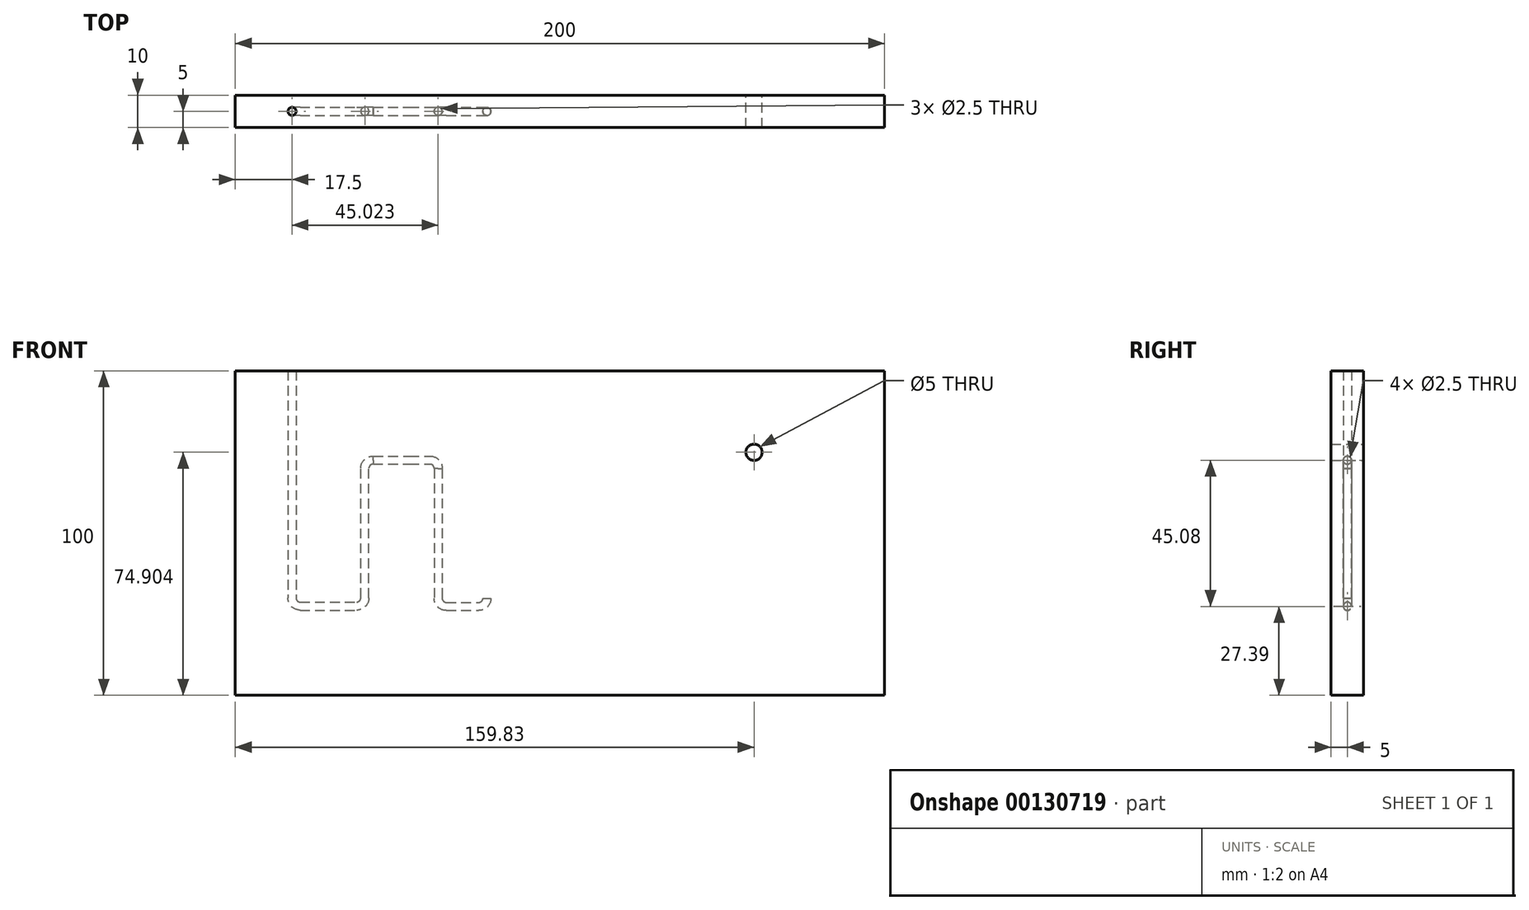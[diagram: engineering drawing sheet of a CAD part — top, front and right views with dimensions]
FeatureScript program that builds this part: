
annotation { "Feature Type Name" : "Feature", "Feature Type Description" : "" }
export const myFeature = defineFeature(function(context is Context, id is Id, definition is map)
    precondition{}
    {
        {
            var Q0;
            Q0=qCreatedBy(makeId("Front.planeOp"),FACE);
            var sketch = newSketch(context, id + "F0", { "sketchPlane" : qUnion([Q0])});
            skLineSegment(sketch, "E0.bottom", {"start": v(100, 50) * mm, "end": v(-100, 50) * mm});
            skLineSegment(sketch, "E0.top", {"start": v(100, -50) * mm, "end": v(-100, -50) * mm});
            skLineSegment(sketch, "E0.left", {"start": v(100, 50) * mm, "end": v(100, -50) * mm});
            skLineSegment(sketch, "E0.right", {"start": v(-100, 50) * mm, "end": v(-100, -50) * mm});
            skPoint(sketch, "E0.middle", {"position": v(0, 0) * mm});
            skLineSegment(sketch, "E1.bottom", {"start": v(95, 45) * mm, "end": v(-95, 45) * mm});
            skLineSegment(sketch, "E1.top", {"start": v(95, -45) * mm, "end": v(-95, -45) * mm});
            skLineSegment(sketch, "E1.left", {"start": v(95, 45) * mm, "end": v(95, -45) * mm});
            skLineSegment(sketch, "E1.right", {"start": v(-95, 45) * mm, "end": v(-95, -45) * mm});
            skLineSegment(sketch, "E2.bottom", {"start": v(40, 22.5) * mm, "end": v(85, 22.5) * mm});
            skLineSegment(sketch, "E2.top", {"start": v(40, -22.5) * mm, "end": v(85, -22.5) * mm});
            skLineSegment(sketch, "E2.left", {"start": v(40, 22.5) * mm, "end": v(40, -22.5) * mm});
            skLineSegment(sketch, "E2.right", {"start": v(85, 22.5) * mm, "end": v(85, -22.5) * mm});
            skLineSegment(sketch, "E3", {"start": v(-82.5, 63.41) * mm, "end": v(-82.5, -18.85) * mm});
            skLineSegment(sketch, "E4", {"start": v(-75.95, -22.5) * mm, "end": v(-62.58, -22.5) * mm});
            skLineSegment(sketch, "E5", {"start": v(-82.5, -18.85) * mm, "end": v(-82.5, -20) * mm});
            skArc(sketch, "E6", {"start": v(-82.5, -20) * mm, "mid": v(-81.77, -21.77) * mm, "end": v(-80, -22.5) * mm});
            skPoint(sketch, "E7.orphan", {"position": v(-82.5, -22.5) * mm});
            skLineSegment(sketch, "E8", {"start": v(-75.95, -22.5) * mm, "end": v(-80, -22.5) * mm});
            skLineSegment(sketch, "E9", {"start": v(-37.48, 9) * mm, "end": v(-37.48, -20.11) * mm});
            skLineSegment(sketch, "E10", {"start": v(-34.98, -22.61) * mm, "end": v(-24.98, -22.61) * mm});
            skArc(sketch, "E11", {"start": v(-37.48, -20.11) * mm, "mid": v(-36.74, -21.88) * mm, "end": v(-34.98, -22.61) * mm});
            skLineSegment(sketch, "E12", {"start": v(-24.98, -22.61) * mm, "end": v(-24.98, -22.61) * mm});
            skLineSegment(sketch, "E13", {"start": v(-22.48, -7.76) * mm, "end": v(-22.48, 19.9) * mm});
            skArc(sketch, "E14", {"start": v(-19.98, 22.4) * mm, "mid": v(-21.74, 21.67) * mm, "end": v(-22.48, 19.9) * mm});
            skPoint(sketch, "E15.orphan", {"position": v(-22.49, 22.48) * mm});
            skPoint(sketch, "E16.endSnap0", {"position": v(-4.99, 24.98) * mm});
            skLineSegment(sketch, "E17", {"start": v(-19.98, 22.4) * mm, "end": v(-7.48, 22.4) * mm});
            skLineSegment(sketch, "E18", {"start": v(-4.98, 19.9) * mm, "end": v(-4.98, -20.1) * mm});
            skArc(sketch, "E19", {"start": v(-4.98, 19.9) * mm, "mid": v(-5.7, 21.67) * mm, "end": v(-7.48, 22.4) * mm});
            skPoint(sketch, "E20.orphan", {"position": v(-4.98, 22.4) * mm});
            skLineSegment(sketch, "E21", {"start": v(-2.48, -22.6) * mm, "end": v(10.02, -22.6) * mm});
            skArc(sketch, "E22", {"start": v(-4.98, -20.1) * mm, "mid": v(-4.24, -21.86) * mm, "end": v(-2.48, -22.6) * mm});
            skPoint(sketch, "E23.orphan", {"position": v(-4.98, -22.6) * mm});
            skArc(sketch, "E24", {"start": v(10.02, -22.6) * mm, "mid": v(11.8, -21.86) * mm, "end": v(12.52, -20.1) * mm});
            skPoint(sketch, "E25.orphan", {"position": v(12.52, -22.6) * mm});
            skArc(sketch, "E26", {"start": v(15.01, 27.39) * mm, "mid": v(13.26, 26.66) * mm, "end": v(12.53, 24.9) * mm});
            skLineSegment(sketch, "E27", {"start": v(15.01, 27.39) * mm, "end": v(59.83, 27.4) * mm});
            skLineSegment(sketch, "E28", {"start": v(12.53, 24.9) * mm, "end": v(12.52, -20.1) * mm});
            skLineSegment(sketch, "E29", {"start": v(62.5, 22.5) * mm, "end": v(62.5, -58.86) * mm});
            skLineSegment(sketch, "E30", {"start": v(-80, -20) * mm, "end": v(-62.5, -20) * mm});
            skLineSegment(sketch, "E31", {"start": v(15.01, 24.9) * mm, "end": v(59.83, 24.9) * mm});
            skCircle(sketch, "E32", {"center": v(59.83, 24.9) * mm, "radius": 2.5 * mm});
            skPoint(sketch, "E33.orphan", {"position": v(62.5, 27.4) * mm});
            skLineSegment(sketch, "E34", {"start": v(-60.08, -20) * mm, "end": v(-60.08, 19.97) * mm});
            skArc(sketch, "E35", {"start": v(-62.58, -22.5) * mm, "mid": v(-60.81, -21.77) * mm, "end": v(-60.08, -20) * mm});
            skArc(sketch, "E36", {"start": v(-60.08, 19.97) * mm, "mid": v(-59.31, 21.78) * mm, "end": v(-57.47, 22.47) * mm});
            skLineSegment(sketch, "E37", {"start": v(-37.48, 9) * mm, "end": v(-37.48, 19.86) * mm});
            skArc(sketch, "E38", {"start": v(-39.97, 22.47) * mm, "mid": v(-38.17, 21.7) * mm, "end": v(-37.48, 19.86) * mm});
            skLineSegment(sketch, "E39", {"start": v(-57.47, 22.47) * mm, "end": v(-52.28, 22.47) * mm});
            skLineSegment(sketch, "E40", {"start": v(-52.28, 22.47) * mm, "end": v(-46.34, 22.47) * mm});
            skLineSegment(sketch, "E41", {"start": v(-46.34, 22.47) * mm, "end": v(-39.97, 22.47) * mm});
            skArc(sketch, "E42", {"start": v(-24.98, -22.61) * mm, "mid": v(-23.2, -21.87) * mm, "end": v(-22.48, -20.1) * mm});
            skLineSegment(sketch, "E43", {"start": v(-22.48, -20.1) * mm, "end": v(-22.48, -7.76) * mm});
            skSolve(sketch);
        }
        {
            var Q0;
            Q0=qCreatedBy(makeId("Top.planeOp"),FACE);
            var Q1;
            Q1=sQuery(id+"F0.wireOp",VERTEX,"E3.start");
            cPlane(context, id + "F1", {"entities" : qUnion([Q0, Q1]), "cplaneType" : CPlaneType.PLANE_POINT, "offset" : 25 * mm, "width" : 150 * mm, "height" : 150 * mm});
        }
        {
            var Q0;
            Q0=qCreatedBy(id+"F1.planeOp",FACE);
            var sketch = newSketch(context, id + "F2", { "sketchPlane" : qUnion([Q0])});
            skCircle(sketch, "E44", {"center": v(-82.5, 0) * mm, "radius": 1.25 * mm});
            skSolve(sketch);
        }
        {
            var Q0;
            {var subQ6=sQuery(id+"F0.wireOp",EDGE,"E0.right");Q0=makeQuery(id+"F0.imprint","IMPRINT",FACE,{"disambiguationData":[TD([[makeQuery(id+"F0.imprint","IMPRINT",EDGE,{"derivedFrom":subQ6}),1.0]])]});}
            var Q1;
            {var subQ4=sQuery(id+"F0.wireOp",EDGE,"E1.right");Q1=makeQuery(id+"F0.imprint","IMPRINT",FACE,{"disambiguationData":[TD([[makeQuery(id+"F0.imprint","IMPRINT",EDGE,{"derivedFrom":subQ4}),1.0]])]});}
            var Q2;
            {var subQ4=sQuery(id+"F0.wireOp",EDGE,"E1.left");Q2=makeQuery(id+"F0.imprint","IMPRINT",FACE,{"disambiguationData":[TD([[makeQuery(id+"F0.imprint","IMPRINT",EDGE,{"derivedFrom":subQ4}),-1.0]])]});}
            var Q3;
            {var subQ4=sQuery(id+"F0.wireOp",EDGE,"E0.left");Q3=makeQuery(id+"F0.imprint","IMPRINT",FACE,{"disambiguationData":[TD([[makeQuery(id+"F0.imprint","IMPRINT",EDGE,{"derivedFrom":subQ4}),-1.0]])]});}
            var Q4;
            {var subQ0=sQuery(id+"F0.wireOp",EDGE,"E2.left");Q4=makeQuery(id+"F0.imprint","IMPRINT",FACE,{"disambiguationData":[TD([[makeQuery(id+"F0.imprint","IMPRINT",EDGE,{"derivedFrom":subQ0}),1.0]])]});}
            var Q5;
            {var subQ0=sQuery(id+"F0.wireOp",EDGE,"E2.right");Q5=makeQuery(id+"F0.imprint","IMPRINT",FACE,{"disambiguationData":[TD([[makeQuery(id+"F0.imprint","IMPRINT",EDGE,{"derivedFrom":subQ0}),-1.0]])]});}
            extrude(context, id + "F3", {"entities" : qUnion([Q0, Q1, Q2, Q3, Q4, Q5]), "endBound" : BoundingType.SYMMETRIC, "depth" : 10 * mm});
        }
        {
            var Q0;
            Q0=makeQuery(id+"F2.imprint","IMPRINT",FACE,{"disambiguationData":[TD([[makeQuery(id+"F2.imprint","IMPRINT",EDGE,{"derivedFrom":sQuery(id+"F2.wireOp",EDGE,"E44")}),1.0]])]});
            var Q1;
            Q1=sQuery(id+"F0.wireOp",EDGE,"E3");
            var Q2;
            Q2=sQuery(id+"F0.wireOp",EDGE,"E5");
            var Q3;
            Q3=sQuery(id+"F0.wireOp",EDGE,"E6");
            var Q4;
            Q4=sQuery(id+"F0.wireOp",EDGE,"E8");
            var Q5;
            Q5=sQuery(id+"F0.wireOp",EDGE,"E4");
            var Q6;
            Q6=sQuery(id+"F0.wireOp",EDGE,"E35");
            var Q7;
            Q7=sQuery(id+"F0.wireOp",EDGE,"E34");
            var Q8;
            Q8=sQuery(id+"F0.wireOp",EDGE,"E36");
            var Q9;
            Q9=sQuery(id+"F0.wireOp",EDGE,"E39");
            var Q10;
            Q10=sQuery(id+"F0.wireOp",EDGE,"E40");
            var Q11;
            Q11=sQuery(id+"F0.wireOp",EDGE,"E38");
            var Q12;
            Q12=sQuery(id+"F0.wireOp",EDGE,"E41");
            var Q13;
            Q13=sQuery(id+"F0.wireOp",EDGE,"E37");
            var Q14;
            Q14=sQuery(id+"F0.wireOp",EDGE,"E9");
            var Q15;
            Q15=sQuery(id+"F0.wireOp",EDGE,"E11");
            var Q16;
            Q16=sQuery(id+"F0.wireOp",EDGE,"E10");
            var Q17;
            Q17=sQuery(id+"F0.wireOp",EDGE,"E42");
            sweep(context, id + "F4", {"operationType" : NewBodyOperationType.REMOVE, "profiles" : qUnion([Q0]), "path" : qUnion([Q1, Q2, Q3, Q4, Q5, Q6, Q7, Q8, Q9, Q10, Q11, Q12, Q13, Q14, Q15, Q16, Q17])});
        }
    });
